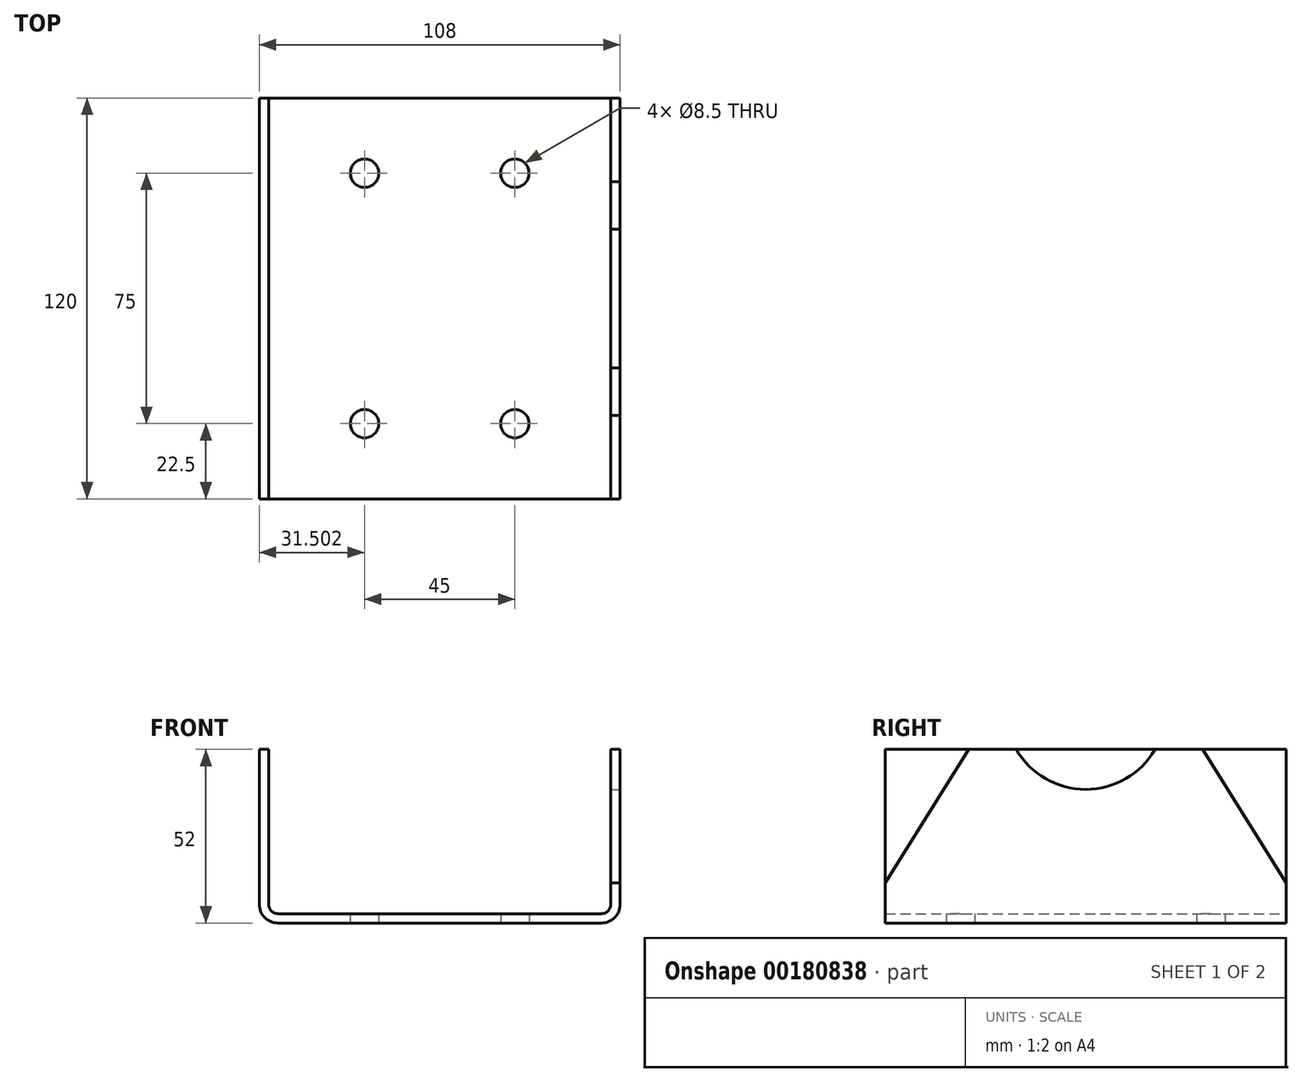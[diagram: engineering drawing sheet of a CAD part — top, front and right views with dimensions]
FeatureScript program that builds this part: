
annotation { "Feature Type Name" : "Feature", "Feature Type Description" : "" }
export const myFeature = defineFeature(function(context is Context, id is Id, definition is map)
    precondition{}
    {
        {
            var Q0;
            Q0=qCreatedBy(makeId("Front.planeOp"),FACE);
            var sketch = newSketch(context, id + "F0", { "sketchPlane" : qUnion([Q0])});
            skLineSegment(sketch, "E0", {"start": v(-44.2, 0) * mm, "end": v(52.6, 0) * mm});
            skLineSegment(sketch, "E1", {"start": v(-49.8, 5.6) * mm, "end": v(-49.8, 52) * mm});
            skPoint(sketch, "E2.visualSharp", {"position": v(-49.8, 0) * mm});
            skArc(sketch, "E2.filletArc", {"start": v(-49.8, 5.6) * mm, "mid": v(-48.17, 1.64) * mm, "end": v(-44.2, 0) * mm});
            skLineSegment(sketch, "E3.0", {"start": v(-47, 5.6) * mm, "end": v(-47, 52) * mm});
            skLineSegment(sketch, "E4.0", {"start": v(-44.2, 2.8) * mm, "end": v(52.6, 2.8) * mm});
            skArc(sketch, "E5.0", {"start": v(-47, 5.6) * mm, "mid": v(-46.19, 3.62) * mm, "end": v(-44.2, 2.8) * mm});
            skLineSegment(sketch, "E6", {"start": v(-49.8, 52) * mm, "end": v(-47, 52) * mm});
            skLineSegment(sketch, "E7", {"start": v(7, 2.8) * mm, "end": v(7, 33.23) * mm});
            skLineSegment(sketch, "E8", {"start": v(58.2, 5.6) * mm, "end": v(58.2, 52) * mm});
            skLineSegment(sketch, "E9", {"start": v(58.2, 52) * mm, "end": v(55.4, 52) * mm});
            skLineSegment(sketch, "E10", {"start": v(55.4, 52) * mm, "end": v(55.4, 5.6) * mm});
            skPoint(sketch, "E11.newPointB", {"position": v(58.2, 2.8) * mm});
            skArc(sketch, "E11.filletArc", {"start": v(52.6, 2.8) * mm, "mid": v(54.57, 3.62) * mm, "end": v(55.4, 5.6) * mm});
            skPoint(sketch, "E12.visualSharp", {"position": v(58.2, 0) * mm});
            skArc(sketch, "E12.filletArc", {"start": v(52.6, 0) * mm, "mid": v(56.55, 1.64) * mm, "end": v(58.2, 5.6) * mm});
            skSolve(sketch);
        }
        {
            var Q0;
            Q0 = qSketchRegion(id + "F0", true);
            extrude(context, id + "F1", {"entities" : qUnion([Q0]), "depth" : 120 * mm});
        }
        {
            var Q0;
            Q0=makeQuery(id+"F1.opExtrude","SWEPT_FACE",FACE,{"disambiguationData":[OSD([sQuery(id+"F0.wireOp",EDGE,"E8")])]});
            var sketch = newSketch(context, id + "F2", { "sketchPlane" : qUnion([Q0])});
            skLineSegment(sketch, "E13", {"start": v(-120, 52) * mm, "end": v(-95, 52) * mm});
            skLineSegment(sketch, "E14", {"start": v(-120, 52) * mm, "end": v(-120, 12) * mm});
            skLineSegment(sketch, "E15", {"start": v(-95, 52) * mm, "end": v(-120, 12) * mm});
            skLineSegment(sketch, "E16", {"start": v(-60, 52) * mm, "end": v(-60, 14.82) * mm});
            skPoint(sketch, "E16.endSnap0", {"position": v(-60, 52) * mm});
            skLineSegment(sketch, "E17.MirrorCS", {"start": v(-25, 52) * mm, "end": v(0, 12) * mm});
            skLineSegment(sketch, "E18.MirrorCS", {"start": v(0, 52) * mm, "end": v(-25, 52) * mm});
            skLineSegment(sketch, "E19.MirrorCS", {"start": v(0, 52) * mm, "end": v(0, 12) * mm});
            skLineSegment(sketch, "E20", {"start": v(-60, 40) * mm, "end": v(-60, 64) * mm});
            skCircle(sketch, "E21", {"center": v(-60, 64) * mm, "radius": 24 * mm});
            skLineSegment(sketch, "E22", {"start": v(-84, 64) * mm, "end": v(-36, 64) * mm});
            skSolve(sketch);
        }
        {
            var Q0;
            Q0 = qSketchRegion(id + "F2", true);
            extrude(context, id + "F3", {"entities" : qUnion([Q0]), "operationType" : NewBodyOperationType.REMOVE, "oppositeDirection" : true, "depth" : 3 * mm});
        }
        {
            var Q0;
            Q0=makeQuery(id+"F1.opExtrude","SWEPT_FACE",FACE,{"disambiguationData":[OSD([sQuery(id+"F0.wireOp",EDGE,"E0")])]});
            var sketch = newSketch(context, id + "F4", { "sketchPlane" : qUnion([Q0])});
            skLineSegment(sketch, "E23", {"start": v(4.2, 120) * mm, "end": v(4.2, 0) * mm});
            skLineSegment(sketch, "E24.0", {"start": v(-44.2, 97.5) * mm, "end": v(52.6, 97.5) * mm});
            skCircle(sketch, "E25", {"center": v(-18.3, 97.5) * mm, "radius": 4.25 * mm});
            skLineSegment(sketch, "E26", {"start": v(-18.3, 97.5) * mm, "end": v(-18.3, 22.5) * mm});
            skCircle(sketch, "E27", {"center": v(-18.3, 22.5) * mm, "radius": 4.25 * mm});
            skCircle(sketch, "E28.MirrorC", {"center": v(26.7, 97.5) * mm, "radius": 4.25 * mm});
            skCircle(sketch, "E29.MirrorC", {"center": v(26.7, 22.5) * mm, "radius": 4.25 * mm});
            skSolve(sketch);
        }
        {
            var Q0;
            Q0 = qSketchRegion(id + "F4", true);
            extrude(context, id + "F5", {"entities" : qUnion([Q0]), "operationType" : NewBodyOperationType.REMOVE, "oppositeDirection" : true, "depth" : 3 * mm});
        }
    });
